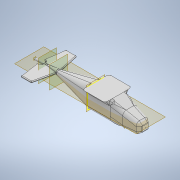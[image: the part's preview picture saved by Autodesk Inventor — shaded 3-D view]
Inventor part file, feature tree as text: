
AUTODESK INVENTOR PART (.ipt)
format: ipt  version: 2021 (Build 250183000, 183)  size: 3,779,072 bytes
history: native  units: mm
features: fillet x14, sketch x12, plane x8, loft x6, other x6, extrude x5, projected_geometry x4
ambient origin geometry x8: Origin, YZ Plane, XZ Plane, XY Plane, X Axis, Y Axis, Z Axis, Center Point
bodies: Solid1 (feature_tree)
feature tree (55):
  sketch  "Sketch1"  dims[d0=884.936mm d1=835.0631mm d2=-901.954mm]
  plane  "Work Plane1"
  sketch  "Sketch2"  dims[d3=1072.134mm d4=93.599mm]
  plane  "Work Plane2"
  sketch  "Sketch3"  dims[d5=1118.87mm d6=-867.918mm d7=1225.296mm]
  plane  "Work Plane3"
  sketch  "Sketch4"  dims[d8=1519.682mm d9=76.581mm d10=-1718.818mm]
  loft  "Loft1"
  fillet  "Fillet1"  [1 undecoded]
  loft  "Loft2"
  loft  "Loft3"
  fillet  "Fillet2"  Radius=1225.296mm
  extrude  "Extrusion1"  Depth=76.581mm
  fillet  "Fillet3"  [1 undecoded]
  plane  "Work Plane4"
  sketch  "Sketch6"  dims[d18=0.0mm d19=90.0deg d20=0.0mm d21=90.0deg]
  sketch  "Sketch7"  dims[d22=0.0mm d23=90.0deg d24=127.0mm d25=254.0mm d26=-6.981317mm]
  extrude  "Extrusion2"  TaperAngle=0.0deg  [1 undecoded]
  fillet  "Fillet4"  Radius=254.0mm
  fillet  "Fillet5"  [1 undecoded]
  loft  "Loft4"
  plane  "Work Plane5"
  loft  "Loft5"
  fillet  "Fillet6"  Radius=254.0mm
  plane  "Work Plane6"
  extrude  "Extrusion3"  Depth=2790.952mm
  fillet  "Fillet7"  Radius=357.378mm
  fillet  "Fillet8"  Radius=1225.296mm
  sketch  "Sketch10"  dims[d34=1.0mm d35=0.0mm d36=381.0mm]
  plane  "Work Plane7"
  loft  "Loft6"
  fillet  "Fillet9"  Radius=759.841mm
  plane  "Work Plane8"
  extrude  "Extrusion4"  Depth=381.0mm
  extrude  "Extrusion5"  TaperAngle=0.0deg  [1 undecoded]
  fillet  "Fillet10"  [1 undecoded]
  fillet  "Fillet11"  Radius=833.882mm
  fillet  "Fillet12"  Radius=153.162mm
  fillet  "Fillet13"  [1 undecoded]
  fillet  "Fillet14"  [1 undecoded]
  other  "Edges1"
  other  "Edges2"
  sketch  "Sketch5"  dims[d11=0.0mm d12=90.0deg d13=0.0mm d14=90.0deg d15=254.0mm d16=0.0mm d17=90.0deg]
  projected_geometry  "Projected Loop1"
  projected_geometry  "Projected Loop2"
  projected_geometry  "Projected Loop3"
  other  "Edges3"
  other  "Edges4"
  sketch  "Sketch8"  dims[d27=50.8mm d28=2790.952mm d29=357.378mm d30=1225.296mm]
  other  "Edges5"
  sketch  "Sketch9"  dims[d31=612.648mm d32=1519.682mm d33=759.841mm]
  sketch  "Sketch11"  dims[d37=254.0mm d38=0.0mm d39=90.0deg d40=0.0mm d41=90.0deg d42=833.882mm d43=153.162mm d44=0.0mm d45=90.0deg d46=0.0mm d47=90.0deg]
  other  "Edges6"
  projected_geometry  "Projected Loop4"
  sketch  "Sketch12"  dims[d48=2189.25mm d49=2000.0mm d50=1225.296mm d51=387.352mm d52=600.0mm d53=600.0mm d54=1713.5mm d55=0.0mm d56=127.0mm d57=983.25mm d58=25.4mm d59=953.008mm d60=0.0mm d61=90.0deg d62=0.0mm d63=90.0deg d64=76.2mm d65=760.0mm d66=361.423629mm d67=411.296529mm d68=205.648265mm d69=180.711815mm d70=473.75mm d71=0.0mm d72=459.486mm d74=459.486mm d75=578.612mm d76=153.162mm d77=289.306mm d78=782.828mm d79=782.828mm d80=3403.6mm d81=1701.8mm d82=340.36mm d83=340.36mm d84=833.882mm d85=2.0mm d86=50.8mm d87=116.9162mm d88=0.0mm d89=50.8mm d90=50.8mm d91=38.1mm d92=38.1mm d93=38.1mm]
note: 8 required parameter values undecoded (feature->parameter linkage not recoverable at this tier; creation-order binding heuristic only, values carry confidence <= 0.55)
